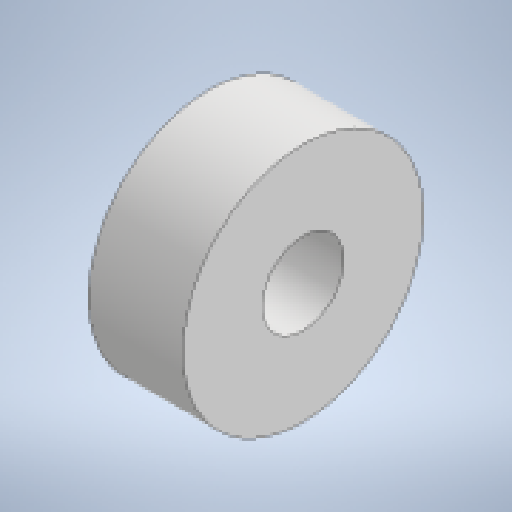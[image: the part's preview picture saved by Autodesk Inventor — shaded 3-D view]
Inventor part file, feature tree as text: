
AUTODESK INVENTOR PART (.ipt)
format: ipt  version: 2023 (Build 270158000, 158)  size: 130,560 bytes
history: native  units: in
note: dims shown in document units (in); Inventor stores cm internally (conversion verified against a paired STEP export)
features: extrude x1, sketch x1
ambient origin geometry x8: Origin, YZ Plane, XZ Plane, XY Plane, X Axis, Y Axis, Z Axis, Center Point
bodies: Solid1 (feature_tree)
feature tree (2):
  extrude  "Extrusion1"  Depth=0.196in
  sketch  "Sketch1"  dims[d0=0.5in d1=0.17in d2=0.196in d3=0.0in]
